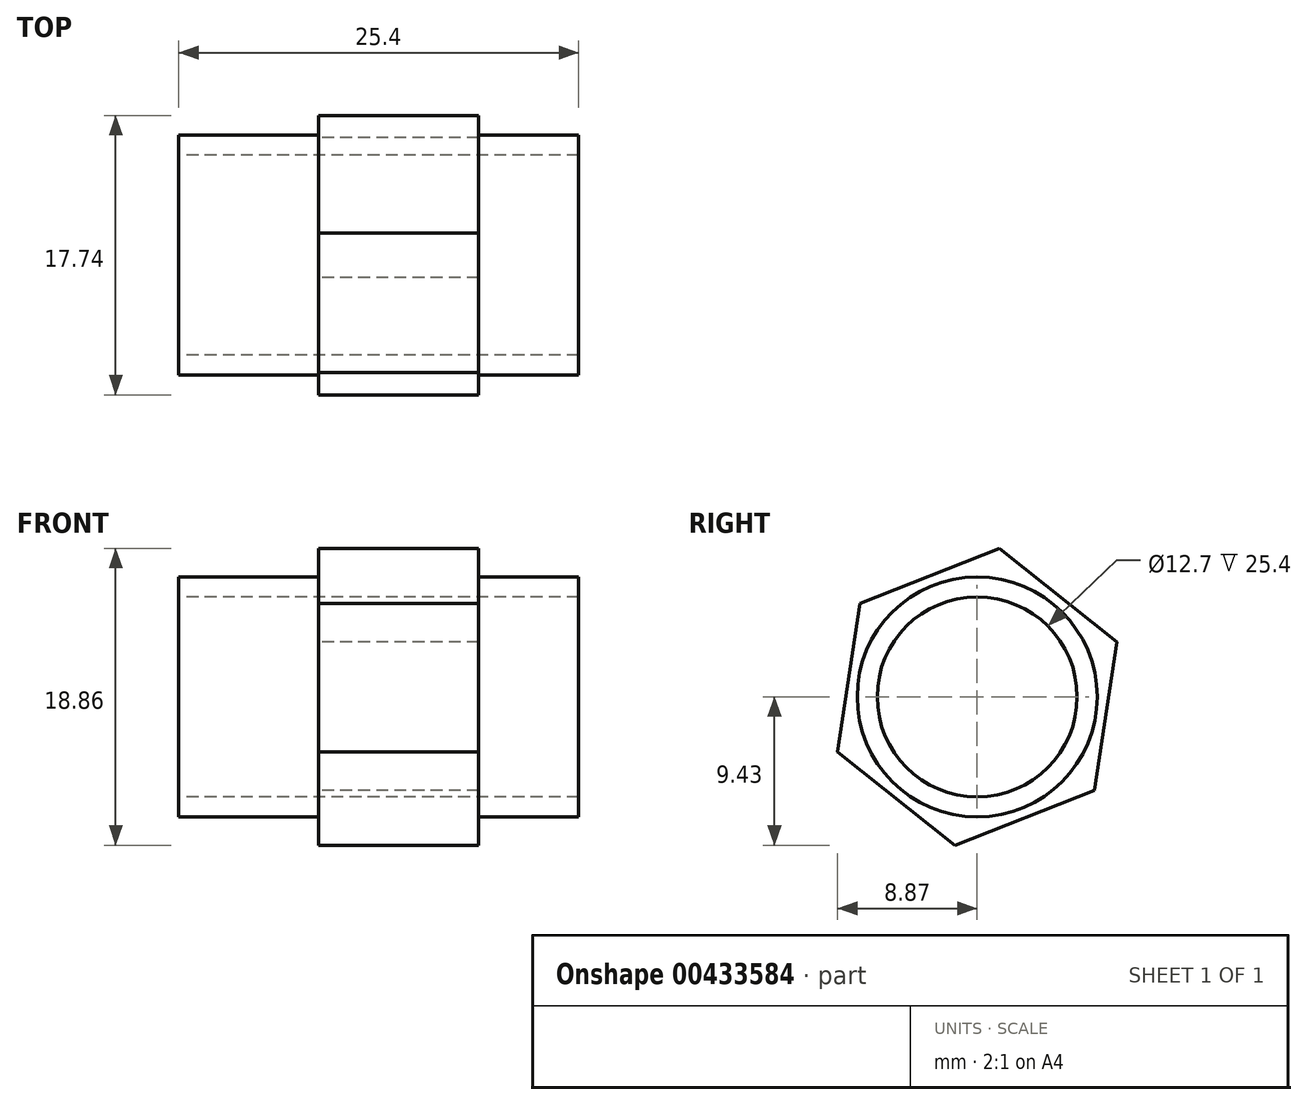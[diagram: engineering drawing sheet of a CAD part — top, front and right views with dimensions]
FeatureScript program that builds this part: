
annotation { "Feature Type Name" : "Feature", "Feature Type Description" : "" }
export const myFeature = defineFeature(function(context is Context, id is Id, definition is map)
    precondition{}
    {
        {
            var Q0;
            Q0=qCreatedBy(makeId("Right.planeOp"),FACE);
            var sketch = newSketch(context, id + "F0", { "sketchPlane" : qUnion([Q0])});
            skCircle(sketch, "E0.cCircle", {"center": v(0, 0) * mm, "radius": 8.26 * mm, "construction": true});
            skLineSegment(sketch, "E0.0", {"start": v(-7.46, 5.94) * mm, "end": v(1.41, 9.43) * mm});
            skLineSegment(sketch, "E0.1", {"start": v(1.41, 9.43) * mm, "end": v(8.87, 3.5) * mm});
            skLineSegment(sketch, "E0.2", {"start": v(8.87, 3.5) * mm, "end": v(7.46, -5.94) * mm});
            skLineSegment(sketch, "E0.3", {"start": v(7.46, -5.94) * mm, "end": v(-1.41, -9.43) * mm});
            skLineSegment(sketch, "E0.4", {"start": v(-1.41, -9.43) * mm, "end": v(-8.87, -3.5) * mm});
            skLineSegment(sketch, "E0.5", {"start": v(-8.87, -3.5) * mm, "end": v(-7.46, 5.94) * mm});
            skPoint(sketch, "E0.0.midPoint", {"position": v(-3.02, 7.68) * mm});
            skSolve(sketch);
        }
        {
            var Q0;
            Q0=makeQuery(id+"F0.imprint","IMPRINT",FACE,{"disambiguationData":[TD([[makeQuery(id+"F0.imprint","IMPRINT",EDGE,{"derivedFrom":sQuery(id+"F0.wireOp",EDGE,"E0.0")}),-1.0]])]});
            extrude(context, id + "F1", {"entities" : qUnion([Q0]), "depth" : 10.16 * mm});
        }
        {
            var Q0;
            Q0=makeQuery(id+"F1.opExtrude","CAP_FACE",FACE,{"disambiguationData":[OSD([sQuery(id+"F0.wireOp",EDGE,"E0.0"),sQuery(id+"F0.wireOp",EDGE,"E0.1"),sQuery(id+"F0.wireOp",EDGE,"E0.2"),sQuery(id+"F0.wireOp",EDGE,"E0.3"),sQuery(id+"F0.wireOp",EDGE,"E0.4"),sQuery(id+"F0.wireOp",EDGE,"E0.5")])],"isStart":false});
            var sketch = newSketch(context, id + "F2", { "sketchPlane" : qUnion([Q0])});
            skCircle(sketch, "E1", {"center": v(0, 0) * mm, "radius": 7.62 * mm});
            skSolve(sketch);
        }
        {
            var Q0;
            Q0=makeQuery(id+"F2.imprint","IMPRINT",FACE,{"disambiguationData":[TD([[makeQuery(id+"F2.imprint","IMPRINT",EDGE,{"derivedFrom":sQuery(id+"F2.wireOp",EDGE,"E1")}),1.0]])]});
            extrude(context, id + "F3", {"entities" : qUnion([Q0]), "operationType" : NewBodyOperationType.ADD, "depth" : 6.35 * mm, "hasSecondDirection" : true, "secondDirectionOppositeDirection" : true, "secondDirectionDepth" : 19.05 * mm});
        }
        {
            var Q0;
            Q0=makeQuery(id+"F3.opExtrude","CAP_FACE",FACE,{"disambiguationData":[OSD([sQuery(id+"F2.wireOp",EDGE,"E1")])],"isStart":true});
            var sketch = newSketch(context, id + "F4", { "sketchPlane" : qUnion([Q0])});
            skCircle(sketch, "E2", {"center": v(0, 0) * mm, "radius": 6.35 * mm});
            skSolve(sketch);
        }
        {
            var Q0;
            Q0=makeQuery(id+"F4.imprint","IMPRINT",FACE,{"disambiguationData":[TD([[makeQuery(id+"F4.imprint","IMPRINT",EDGE,{"derivedFrom":sQuery(id+"F4.wireOp",EDGE,"E2")}),1.0]])]});
            extrude(context, id + "F5", {"entities" : qUnion([Q0]), "operationType" : NewBodyOperationType.REMOVE, "endBound" : BoundingType.THROUGH_ALL, "oppositeDirection" : true, "depth" : 25.4 * mm});
        }
    });
